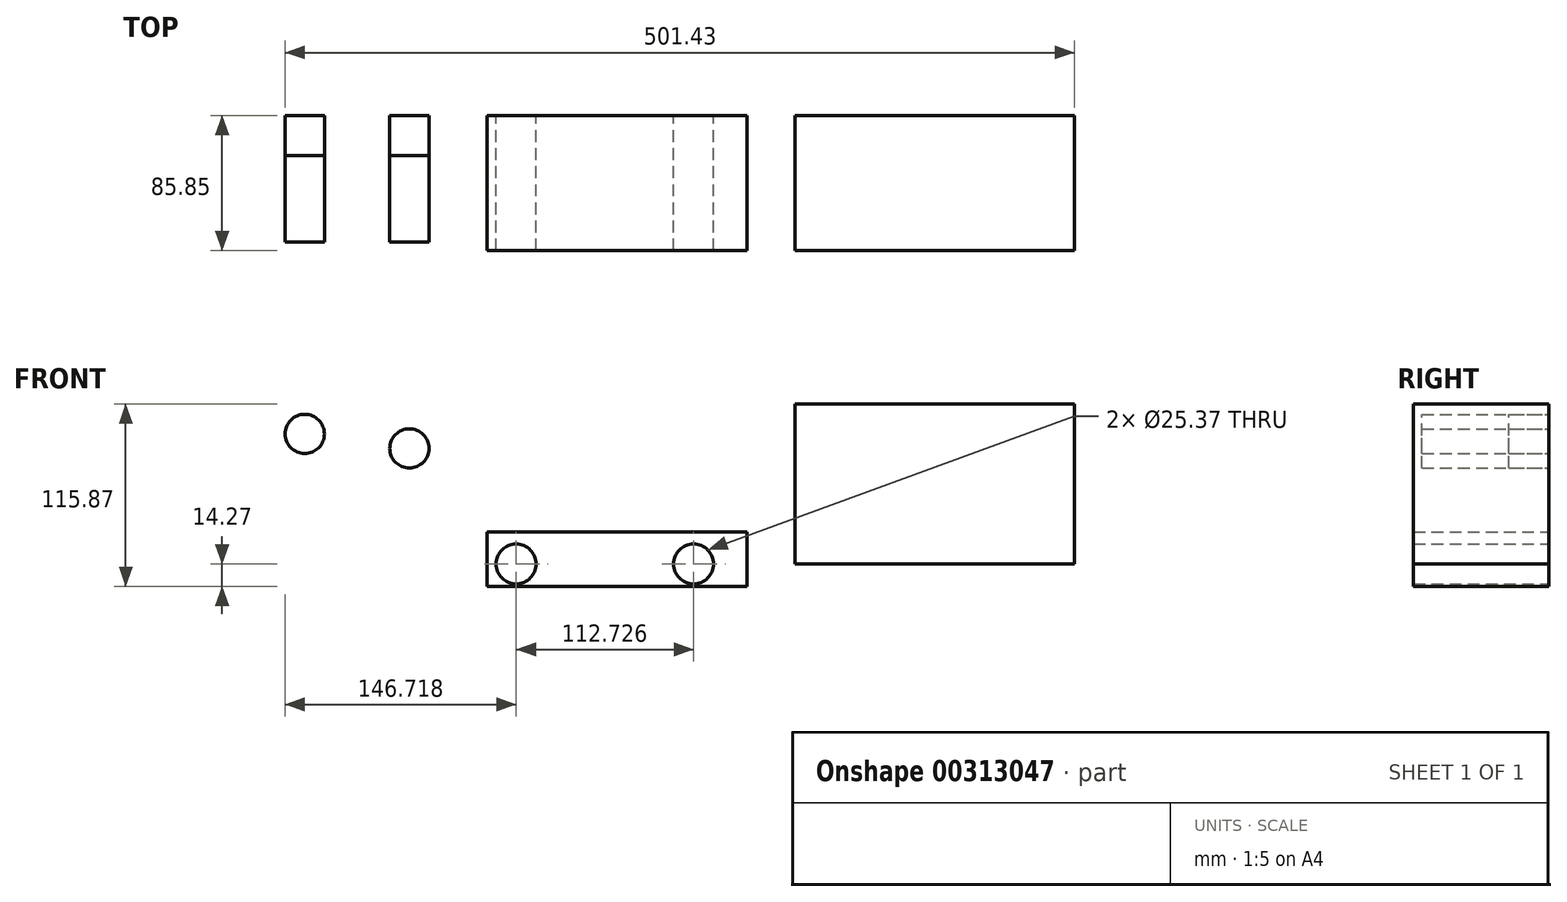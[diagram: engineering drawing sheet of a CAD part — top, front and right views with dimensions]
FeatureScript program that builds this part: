
annotation { "Feature Type Name" : "Feature", "Feature Type Description" : "" }
export const myFeature = defineFeature(function(context is Context, id is Id, definition is map)
    precondition{}
    {
        {
            var Q0;
            Q0=qCreatedBy(makeId("Front.planeOp"),FACE);
            var sketch = newSketch(context, id + "F0", { "sketchPlane" : qUnion([Q0])});
            skLineSegment(sketch, "E0.bottom", {"start": v(-157.53, 20.48) * mm, "end": v(7.57, 20.48) * mm});
            skLineSegment(sketch, "E0.top", {"start": v(-157.53, -14.27) * mm, "end": v(7.57, -14.27) * mm});
            skLineSegment(sketch, "E0.left", {"start": v(-157.53, 20.48) * mm, "end": v(-157.53, -14.27) * mm});
            skLineSegment(sketch, "E0.right", {"start": v(7.57, 20.48) * mm, "end": v(7.57, -14.27) * mm});
            skLineSegment(sketch, "E1.bottom", {"start": v(38.26, 0) * mm, "end": v(215.8, 0) * mm});
            skLineSegment(sketch, "E1.top", {"start": v(38.26, 101.6) * mm, "end": v(215.8, 101.6) * mm});
            skLineSegment(sketch, "E1.left", {"start": v(38.26, 0) * mm, "end": v(38.26, 101.6) * mm});
            skLineSegment(sketch, "E1.right", {"start": v(215.8, 0) * mm, "end": v(215.8, 101.6) * mm});
            skCircle(sketch, "E2", {"center": v(-138.9, 0) * mm, "radius": 12.69 * mm});
            skCircle(sketch, "E3", {"center": v(-26.18, 0) * mm, "radius": 12.69 * mm});
            skSolve(sketch);
        }
        {
            var Q0;
            Q0 = qSketchRegion(id + "F0", true);
            extrude(context, id + "F1", {"entities" : qUnion([Q0]), "depth" : 85.85 * mm});
        }
        {
            var Q0;
            Q0=qCreatedBy(makeId("Front.planeOp"),FACE);
            var sketch = newSketch(context, id + "F2", { "sketchPlane" : qUnion([Q0])});
            skCircle(sketch, "E4", {"center": v(-206.73, 73.4) * mm, "radius": 12.45 * mm});
            skCircle(sketch, "E5", {"center": v(-273.18, 82.6) * mm, "radius": 12.45 * mm});
            skSolve(sketch);
        }
        {
            var Q0;
            Q0 = qSketchRegion(id + "F2", true);
            extrude(context, id + "F3", {"entities" : qUnion([Q0]), "depth" : 80.52 * mm});
        }
        {
            var Q0;
            Q0 = qSketchRegion(id + "F2", true);
            extrude(context, id + "F4", {"entities" : qUnion([Q0]), "depth" : 25.4 * mm});
        }
    });
